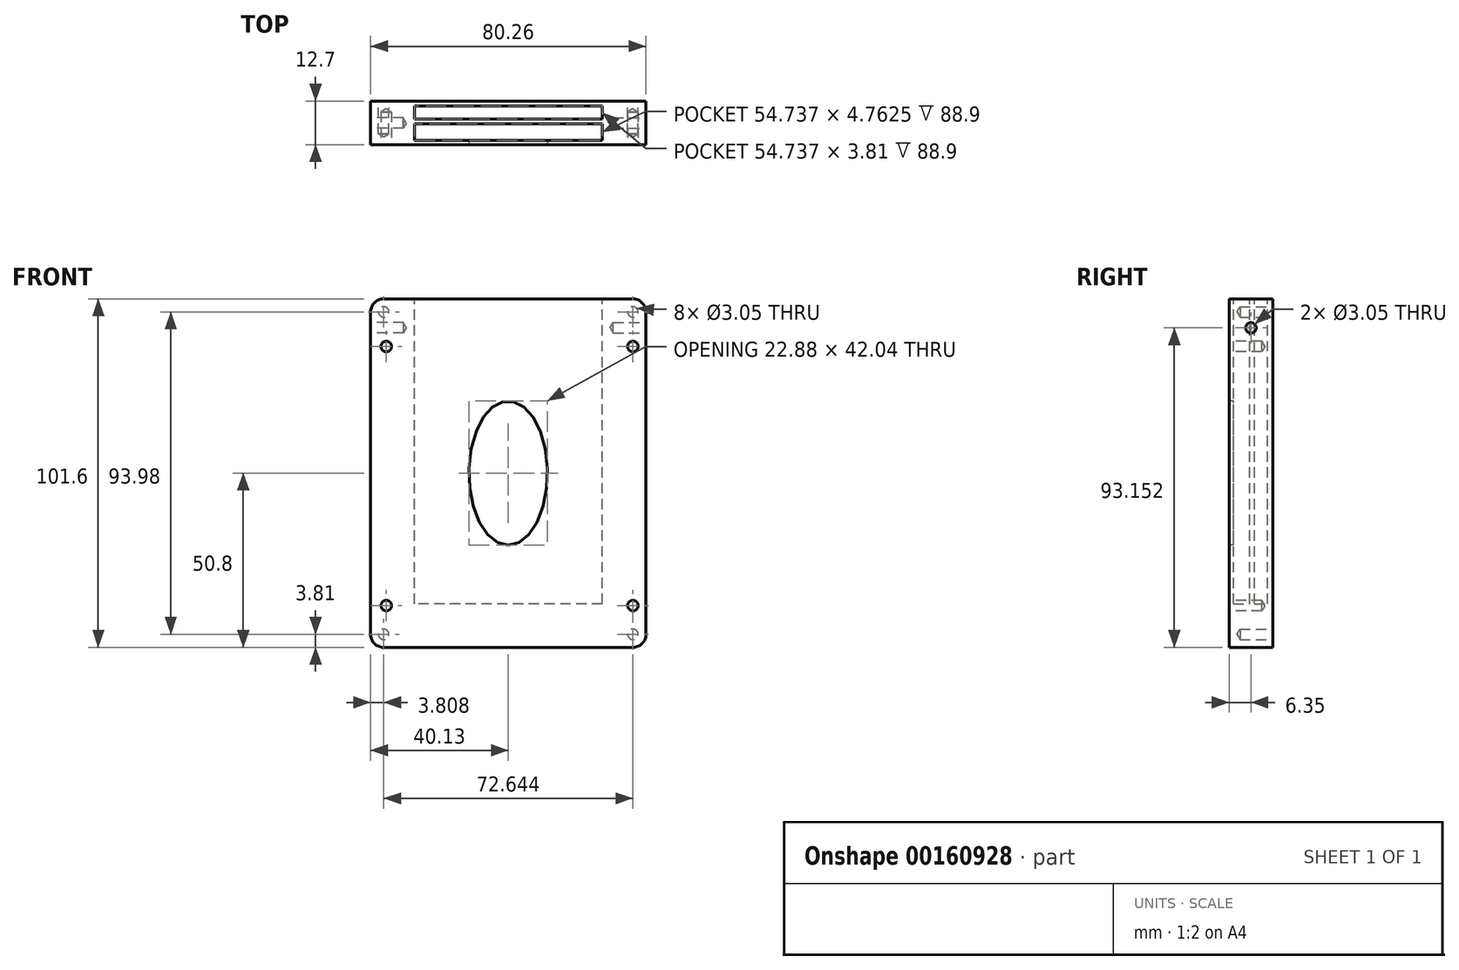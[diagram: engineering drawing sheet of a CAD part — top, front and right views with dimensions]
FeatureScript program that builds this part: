
annotation { "Feature Type Name" : "Feature", "Feature Type Description" : "" }
export const myFeature = defineFeature(function(context is Context, id is Id, definition is map)
    precondition{}
    {
        {
            var Q0;
            Q0=qCreatedBy(makeId("Front.planeOp"),FACE);
            var sketch = newSketch(context, id + "F0", { "sketchPlane" : qUnion([Q0])});
            skLineSegment(sketch, "E0.bottom", {"start": v(-40.13, 50.8) * mm, "end": v(40.13, 50.8) * mm});
            skLineSegment(sketch, "E0.top", {"start": v(-40.13, -50.8) * mm, "end": v(40.13, -50.8) * mm});
            skLineSegment(sketch, "E0.left", {"start": v(-40.13, 50.8) * mm, "end": v(-40.13, -50.8) * mm});
            skLineSegment(sketch, "E0.right", {"start": v(40.13, 50.8) * mm, "end": v(40.13, -50.8) * mm});
            skPoint(sketch, "E0.middle", {"position": v(0, 0) * mm});
            skSolve(sketch);
        }
        {
            var Q0;
            Q0 = qSketchRegion(id + "F0", true);
            extrude(context, id + "F1", {"entities" : qUnion([Q0]), "endBound" : BoundingType.SYMMETRIC, "depth" : 12.7 * mm});
        }
        {
            var Q0;
            Q0=makeQuery(id+"F1.opExtrude","SWEPT_FACE",FACE,{"disambiguationData":[OSD([sQuery(id+"F0.wireOp",EDGE,"E0.bottom")])]});
            var sketch = newSketch(context, id + "F2", { "sketchPlane" : qUnion([Q0])});
            skLineSegment(sketch, "E1.bottom", {"start": v(27.37, -5.08) * mm, "end": v(-27.37, -5.08) * mm});
            skLineSegment(sketch, "E1.top", {"start": v(27.37, -0.32) * mm, "end": v(-27.37, -0.32) * mm});
            skLineSegment(sketch, "E1.left", {"start": v(27.37, -5.08) * mm, "end": v(27.37, -0.32) * mm});
            skLineSegment(sketch, "E1.right", {"start": v(-27.37, -5.08) * mm, "end": v(-27.37, -0.32) * mm});
            skPoint(sketch, "E1.middle", {"position": v(0, -2.7) * mm});
            skSolve(sketch);
        }
        {
            var Q0;
            Q0 = qSketchRegion(id + "F2", true);
            extrude(context, id + "F3", {"entities" : qUnion([Q0]), "operationType" : NewBodyOperationType.REMOVE, "oppositeDirection" : true, "depth" : 88.9 * mm});
        }
        {
            var Q0;
            Q0=makeQuery(id+"F1.opExtrude","CAP_FACE",FACE,{"disambiguationData":[OSD([sQuery(id+"F0.wireOp",EDGE,"E0.bottom"),sQuery(id+"F0.wireOp",EDGE,"E0.top"),sQuery(id+"F0.wireOp",EDGE,"E0.left"),sQuery(id+"F0.wireOp",EDGE,"E0.right")])],"isStart":false});
            var sketch = newSketch(context, id + "F4", { "sketchPlane" : qUnion([Q0])});
            skEllipse(sketch, "E2", {"center": v(0, 0) * mm, "majorRadius": 21.02 * mm, "minorRadius": 11.44 * mm, "majorAxis": v(0, -1)});
            skSolve(sketch);
        }
        {
            var Q0;
            Q0 = qSketchRegion(id + "F4", true);
            extrude(context, id + "F5", {"entities" : qUnion([Q0]), "operationType" : NewBodyOperationType.REMOVE, "oppositeDirection" : true, "depth" : 5.08 * mm});
        }
        {
            var Q0;
            Q0=makeQuery(id+"F1.opExtrude","SWEPT_FACE",FACE,{"disambiguationData":[OSD([sQuery(id+"F0.wireOp",EDGE,"E0.bottom")])]});
            var sketch = newSketch(context, id + "F6", { "sketchPlane" : qUnion([Q0])});
            skLineSegment(sketch, "E3.bottom", {"start": v(27.37, 1.08) * mm, "end": v(-27.37, 1.08) * mm});
            skLineSegment(sketch, "E3.top", {"start": v(27.37, 4.89) * mm, "end": v(-27.37, 4.89) * mm});
            skLineSegment(sketch, "E3.left", {"start": v(27.37, 1.08) * mm, "end": v(27.37, 4.89) * mm});
            skLineSegment(sketch, "E3.right", {"start": v(-27.37, 1.08) * mm, "end": v(-27.37, 4.89) * mm});
            skPoint(sketch, "E3.middle", {"position": v(0, 2.98) * mm});
            skSolve(sketch);
        }
        {
            var Q0;
            Q0 = qSketchRegion(id + "F6", true);
            extrude(context, id + "F7", {"entities" : qUnion([Q0]), "operationType" : NewBodyOperationType.REMOVE, "oppositeDirection" : true, "depth" : 88.9 * mm});
        }
        {
            var Q0;
            Q0=makeQuery(id+"F1.opExtrude","SWEPT_EDGE",EDGE,{"disambiguationData":[OSD([sQuery(id+"F0.wireOp",EDGE,"E0.bottom"),sQuery(id+"F0.wireOp",EDGE,"E0.right")])]});
            var Q1;
            Q1=makeQuery(id+"F1.opExtrude","SWEPT_EDGE",EDGE,{"disambiguationData":[OSD([sQuery(id+"F0.wireOp",EDGE,"E0.bottom"),sQuery(id+"F0.wireOp",EDGE,"E0.left")])]});
            var Q2;
            Q2=makeQuery(id+"F1.opExtrude","SWEPT_EDGE",EDGE,{"disambiguationData":[OSD([sQuery(id+"F0.wireOp",EDGE,"E0.top"),sQuery(id+"F0.wireOp",EDGE,"E0.left")])]});
            var Q3;
            Q3=makeQuery(id+"F1.opExtrude","SWEPT_EDGE",EDGE,{"disambiguationData":[OSD([sQuery(id+"F0.wireOp",EDGE,"E0.top"),sQuery(id+"F0.wireOp",EDGE,"E0.right")])]});
            fillet(context, id + "F8", {"entities" : qUnion([Q0, Q1, Q2, Q3]), "radius" : 3.8 * mm, "tangentPropagation" : true, "allowEdgeOverflow" : false});
        }
        {
            var Q0;
            Q0=makeQuery(id+"F1.opExtrude","SWEPT_FACE",FACE,{"disambiguationData":[OSD([sQuery(id+"F0.wireOp",EDGE,"E0.left")])]});
            var sketch = newSketch(context, id + "F9", { "sketchPlane" : qUnion([Q0])});
            skPoint(sketch, "E4", {"position": v(0, 42.35) * mm});
            skSolve(sketch);
        }
        {
            var Q0;
            Q0=sQuery(id+"F9.wireOp",VERTEX,"E4");
            var Q1;
            Q1=makeQuery(id+"F1.opExtrude","SWEPT_BODY",BODY,{"disambiguationData":[OSD([sQuery(id+"F0.wireOp",EDGE,"E0.bottom"),sQuery(id+"F0.wireOp",EDGE,"E0.top"),sQuery(id+"F0.wireOp",EDGE,"E0.left"),sQuery(id+"F0.wireOp",EDGE,"E0.right")])]});
            hole(context, id + "F10", {"style" : HoleStyle.SIMPLE, "endStyle" : HoleEndStyle.BLIND, "holeDiameter" : 3.05 * mm, "holeDepth" : 9.52 * mm, "locations" : qUnion([Q0]), "scope" : qUnion([Q1])});
        }
        {
            var Q0;
            Q0=makeQuery(id+"F1.opExtrude","SWEPT_FACE",FACE,{"disambiguationData":[OSD([sQuery(id+"F0.wireOp",EDGE,"E0.right")])]});
            var sketch = newSketch(context, id + "F11", { "sketchPlane" : qUnion([Q0])});
            skPoint(sketch, "E5", {"position": v(0, 42.35) * mm});
            skPoint(sketch, "E5.positionSnap0", {"position": v(0, 47) * mm});
            skSolve(sketch);
        }
        {
            var Q0;
            Q0=sQuery(id+"F11.wireOp",VERTEX,"E5");
            var Q1;
            Q1=makeQuery(id+"F1.opExtrude","SWEPT_BODY",BODY,{"disambiguationData":[OSD([sQuery(id+"F0.wireOp",EDGE,"E0.bottom"),sQuery(id+"F0.wireOp",EDGE,"E0.top"),sQuery(id+"F0.wireOp",EDGE,"E0.left"),sQuery(id+"F0.wireOp",EDGE,"E0.right")])]});
            hole(context, id + "F12", {"style" : HoleStyle.SIMPLE, "endStyle" : HoleEndStyle.BLIND, "holeDiameter" : 3.05 * mm, "holeDepth" : 9.52 * mm, "locations" : qUnion([Q0]), "scope" : qUnion([Q1])});
        }
        {
            var Q0;
            Q0=makeQuery(id+"F1.opExtrude","CAP_FACE",FACE,{"disambiguationData":[OSD([sQuery(id+"F0.wireOp",EDGE,"E0.bottom"),sQuery(id+"F0.wireOp",EDGE,"E0.top"),sQuery(id+"F0.wireOp",EDGE,"E0.left"),sQuery(id+"F0.wireOp",EDGE,"E0.right")])],"isStart":true});
            var sketch = newSketch(context, id + "F13", { "sketchPlane" : qUnion([Q0])});
            skPoint(sketch, "E6", {"position": v(-36.32, 47) * mm});
            skPoint(sketch, "E7", {"position": v(36.32, 47) * mm});
            skPoint(sketch, "E8", {"position": v(36.32, -47) * mm});
            skPoint(sketch, "E9", {"position": v(-36.32, -47) * mm});
            skSolve(sketch);
        }
        {
            var Q0;
            Q0=sQuery(id+"F13.wireOp",VERTEX,"E6");
            var Q1;
            Q1=sQuery(id+"F13.wireOp",VERTEX,"E7");
            var Q2;
            Q2=sQuery(id+"F13.wireOp",VERTEX,"E9");
            var Q3;
            Q3=sQuery(id+"F13.wireOp",VERTEX,"E8");
            var Q4;
            Q4=makeQuery(id+"F1.opExtrude","SWEPT_BODY",BODY,{"disambiguationData":[OSD([sQuery(id+"F0.wireOp",EDGE,"E0.bottom"),sQuery(id+"F0.wireOp",EDGE,"E0.top"),sQuery(id+"F0.wireOp",EDGE,"E0.left"),sQuery(id+"F0.wireOp",EDGE,"E0.right")])]});
            hole(context, id + "F14", {"style" : HoleStyle.SIMPLE, "endStyle" : HoleEndStyle.BLIND, "holeDiameter" : 3.05 * mm, "holeDepth" : 9.52 * mm, "locations" : qUnion([Q0, Q1, Q2, Q3]), "scope" : qUnion([Q4])});
        }
        {
            var Q0;
            Q0=makeQuery(id+"F1.opExtrude","CAP_FACE",FACE,{"disambiguationData":[OSD([sQuery(id+"F0.wireOp",EDGE,"E0.bottom"),sQuery(id+"F0.wireOp",EDGE,"E0.top"),sQuery(id+"F0.wireOp",EDGE,"E0.left"),sQuery(id+"F0.wireOp",EDGE,"E0.right")])],"isStart":false});
            var sketch = newSketch(context, id + "F15", { "sketchPlane" : qUnion([Q0])});
            skPoint(sketch, "E10", {"position": v(-35.57, 36.93) * mm});
            skPoint(sketch, "E11", {"position": v(36.32, 36.93) * mm});
            skPoint(sketch, "E12", {"position": v(-35.57, -38.61) * mm});
            skPoint(sketch, "E13", {"position": v(36.32, -38.61) * mm});
            skSolve(sketch);
        }
        {
            var Q0;
            Q0=sQuery(id+"F15.wireOp",VERTEX,"E10");
            var Q1;
            Q1=sQuery(id+"F15.wireOp",VERTEX,"E12");
            var Q2;
            Q2=sQuery(id+"F15.wireOp",VERTEX,"E13");
            var Q3;
            Q3=sQuery(id+"F15.wireOp",VERTEX,"E11");
            var Q4;
            Q4=makeQuery(id+"F1.opExtrude","SWEPT_BODY",BODY,{"disambiguationData":[OSD([sQuery(id+"F0.wireOp",EDGE,"E0.bottom"),sQuery(id+"F0.wireOp",EDGE,"E0.top"),sQuery(id+"F0.wireOp",EDGE,"E0.left"),sQuery(id+"F0.wireOp",EDGE,"E0.right")])]});
            hole(context, id + "F16", {"style" : HoleStyle.SIMPLE, "endStyle" : HoleEndStyle.BLIND, "holeDiameter" : 3.05 * mm, "holeDepth" : 9.52 * mm, "locations" : qUnion([Q0, Q1, Q2, Q3]), "scope" : qUnion([Q4])});
        }
    });
